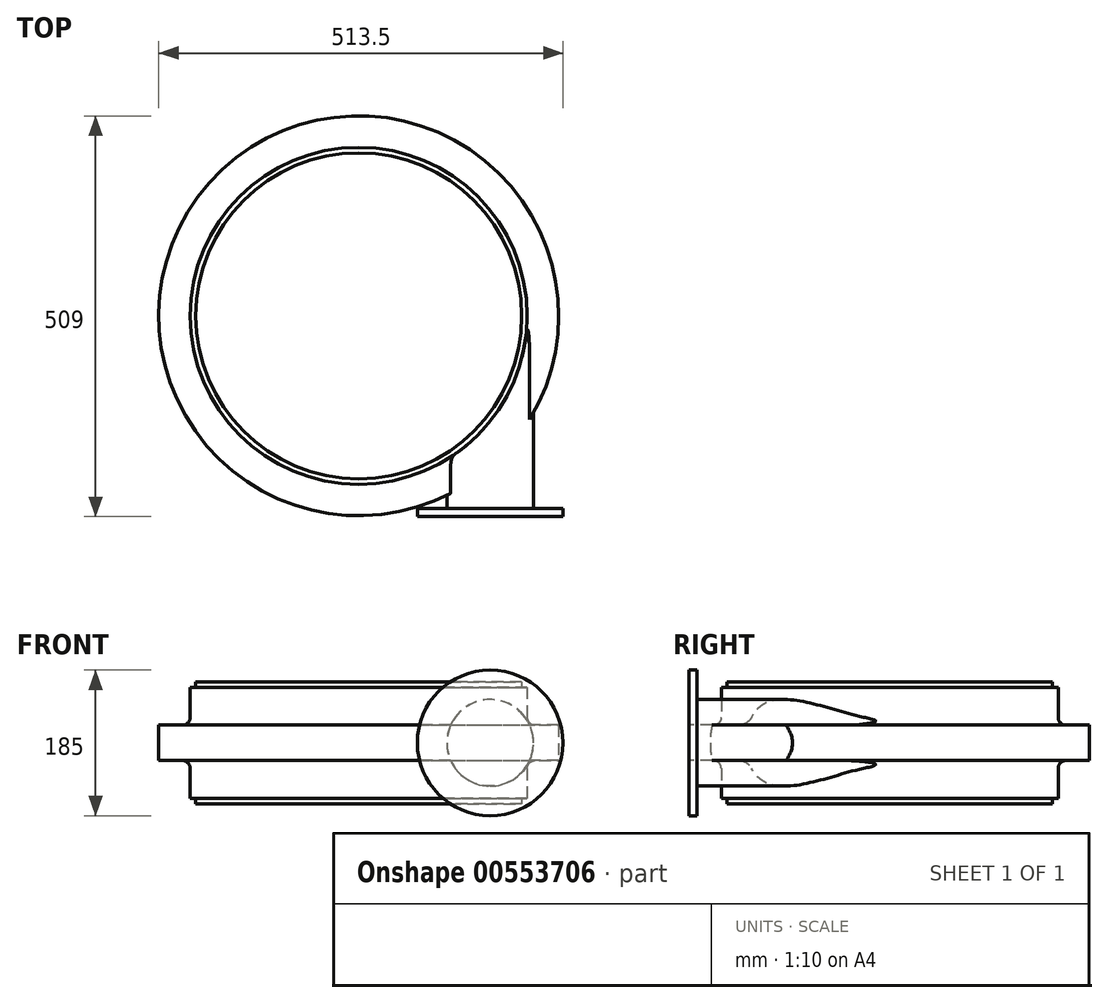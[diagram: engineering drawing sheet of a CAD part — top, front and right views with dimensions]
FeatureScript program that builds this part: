
annotation { "Feature Type Name" : "Feature", "Feature Type Description" : "" }
export const myFeature = defineFeature(function(context is Context, id is Id, definition is map)
    precondition{}
    {
        {
            var Q0;
            Q0=qCreatedBy(makeId("Front.planeOp"),FACE);
            var sketch = newSketch(context, id + "F0", { "sketchPlane" : qUnion([Q0])});
            skLineSegment(sketch, "E0", {"start": v(0, 0) * mm, "end": v(0, 155) * mm});
            skLineSegment(sketch, "E1", {"start": v(0, 155) * mm, "end": v(207, 155) * mm});
            skLineSegment(sketch, "E2", {"start": v(254, 100) * mm, "end": v(254, 55) * mm});
            skLineSegment(sketch, "E3", {"start": v(207, 0) * mm, "end": v(0, 0) * mm});
            skLineSegment(sketch, "E4", {"start": v(214, 148) * mm, "end": v(214, 110) * mm});
            skLineSegment(sketch, "E5", {"start": v(224, 100) * mm, "end": v(254, 100) * mm});
            skLineSegment(sketch, "E6", {"start": v(214, 7) * mm, "end": v(214, 45) * mm});
            skLineSegment(sketch, "E7", {"start": v(224, 55) * mm, "end": v(254, 55) * mm});
            skPoint(sketch, "E8.orphan", {"position": v(254, 0) * mm});
            skPoint(sketch, "E9.visualSharp", {"position": v(214, 55) * mm});
            skArc(sketch, "E9.filletArc", {"start": v(224, 55) * mm, "mid": v(216.93, 52.07) * mm, "end": v(214, 45) * mm});
            skPoint(sketch, "E10.visualSharp", {"position": v(214, 100) * mm});
            skArc(sketch, "E10.filletArc", {"start": v(214, 110) * mm, "mid": v(216.93, 102.93) * mm, "end": v(224, 100) * mm});
            skLineSegment(sketch, "E11.top", {"start": v(214, 148) * mm, "end": v(207, 148) * mm});
            skLineSegment(sketch, "E11.right", {"start": v(207, 155) * mm, "end": v(207, 148) * mm});
            skPoint(sketch, "E12.orphan", {"position": v(214, 155) * mm});
            skLineSegment(sketch, "E13.top", {"start": v(214, 7) * mm, "end": v(207, 7) * mm});
            skLineSegment(sketch, "E13.right", {"start": v(207, 0) * mm, "end": v(207, 7) * mm});
            skPoint(sketch, "E14.orphan", {"position": v(214, 0) * mm});
            skSolve(sketch);
        }
        {
            var Q0;
            Q0=makeQuery(id+"F0.imprint","IMPRINT",FACE,{"disambiguationData":[TD([[makeQuery(id+"F0.imprint","IMPRINT",EDGE,{"derivedFrom":sQuery(id+"F0.wireOp",EDGE,"E0")}),-1.0]])]});
            var Q1;
            Q1=sQuery(id+"F0.wireOp",EDGE,"E0");
            revolve(context, id + "F1", {"entities" : qUnion([Q0]), "axis" : qUnion([Q1]), "revolveType" : RevolveType.FULL});
        }
        {
            var Q0;
            Q0=qCreatedBy(makeId("Front.planeOp"),FACE);
            var sketch = newSketch(context, id + "F2", { "sketchPlane" : qUnion([Q0])});
            skCircle(sketch, "E15", {"center": v(167, 77.5) * mm, "radius": 55 * mm});
            skSolve(sketch);
        }
        {
            var Q0;
            Q0=makeQuery(id+"F2.imprint","IMPRINT",FACE,{"disambiguationData":[TD([[makeQuery(id+"F2.imprint","IMPRINT",EDGE,{"derivedFrom":sQuery(id+"F2.wireOp",EDGE,"E15")}),1.0]])]});
            extrude(context, id + "F3", {"entities" : qUnion([Q0]), "operationType" : NewBodyOperationType.ADD, "depth" : 245 * mm, "offsetDistance" : 25 * mm});
        }
        {
            var Q0;
            Q0=makeQuery(id+"F3.opExtrude","CAP_FACE",FACE,{"disambiguationData":[OSD([sQuery(id+"F2.wireOp",EDGE,"E15")])],"isStart":false});
            var sketch = newSketch(context, id + "F4", { "sketchPlane" : qUnion([Q0])});
            skCircle(sketch, "E16.0.0", {"center": v(167, 77.5) * mm, "radius": 55 * mm});
            skCircle(sketch, "E17", {"center": v(167, 77.5) * mm, "radius": 92.5 * mm});
            skSolve(sketch);
        }
        {
            var Q0;
            Q0=makeQuery(id+"F4.imprint","IMPRINT",FACE,{"disambiguationData":[TD([[makeQuery(id+"F4.imprint","IMPRINT",EDGE,{"derivedFrom":sQuery(id+"F4.wireOp",EDGE,"E16.0.0")}),-1.0]])]});
            var Q1;
            Q1=makeQuery(id+"F4.imprint","IMPRINT",FACE,{"disambiguationData":[TD([[makeQuery(id+"F4.imprint","IMPRINT",EDGE,{"derivedFrom":sQuery(id+"F4.wireOp",EDGE,"E16.0.0")}),1.0]])]});
            extrude(context, id + "F5", {"entities" : qUnion([Q0, Q1]), "operationType" : NewBodyOperationType.ADD, "depth" : 10 * mm, "offsetDistance" : 25 * mm});
        }
    });
